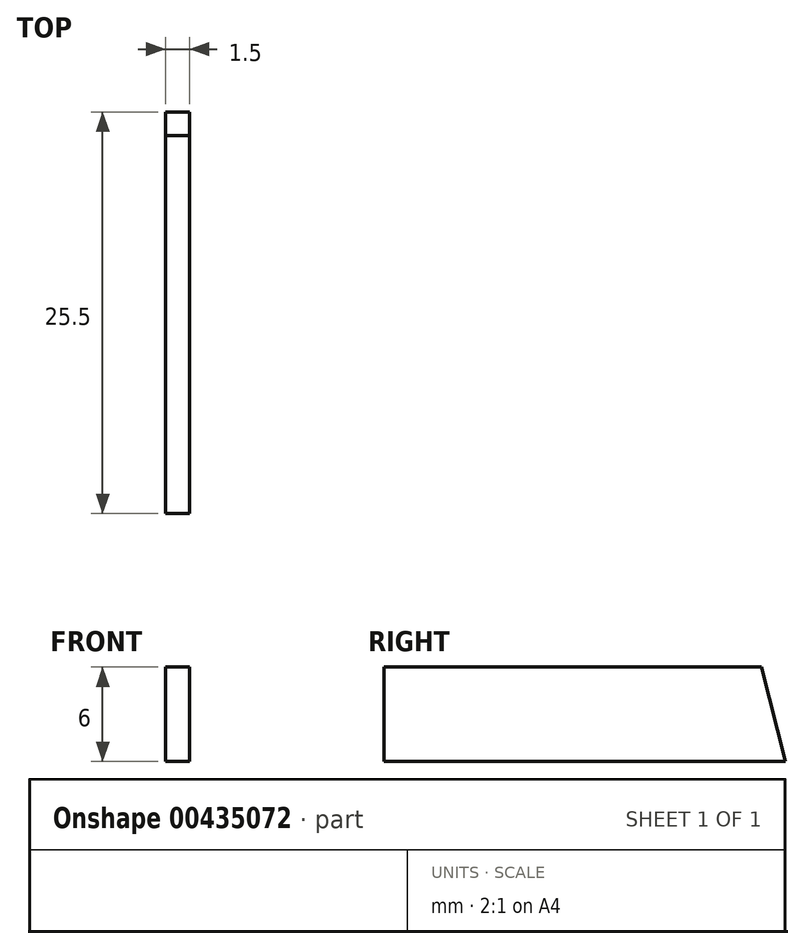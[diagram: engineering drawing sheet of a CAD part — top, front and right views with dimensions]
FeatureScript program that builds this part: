
annotation { "Feature Type Name" : "Feature", "Feature Type Description" : "" }
export const myFeature = defineFeature(function(context is Context, id is Id, definition is map)
    precondition{}
    {
        {
            var Q0;
            Q0=qCreatedBy(makeId("Right.planeOp"),FACE);
            var sketch = newSketch(context, id + "F0", { "sketchPlane" : qUnion([Q0])});
            skLineSegment(sketch, "E0", {"start": v(0, 0) * mm, "end": v(0, 6) * mm});
            skLineSegment(sketch, "E1", {"start": v(0, 6) * mm, "end": v(24, 6) * mm});
            skLineSegment(sketch, "E2", {"start": v(24, 6) * mm, "end": v(25.5, 0) * mm});
            skLineSegment(sketch, "E3", {"start": v(25.5, 0) * mm, "end": v(0, 0) * mm});
            skSolve(sketch);
        }
        {
            var Q0;
            Q0 = qSketchRegion(id + "F0", true);
            extrude(context, id + "F1", {"entities" : qUnion([Q0]), "depth" : 1.5 * mm});
        }
    });
